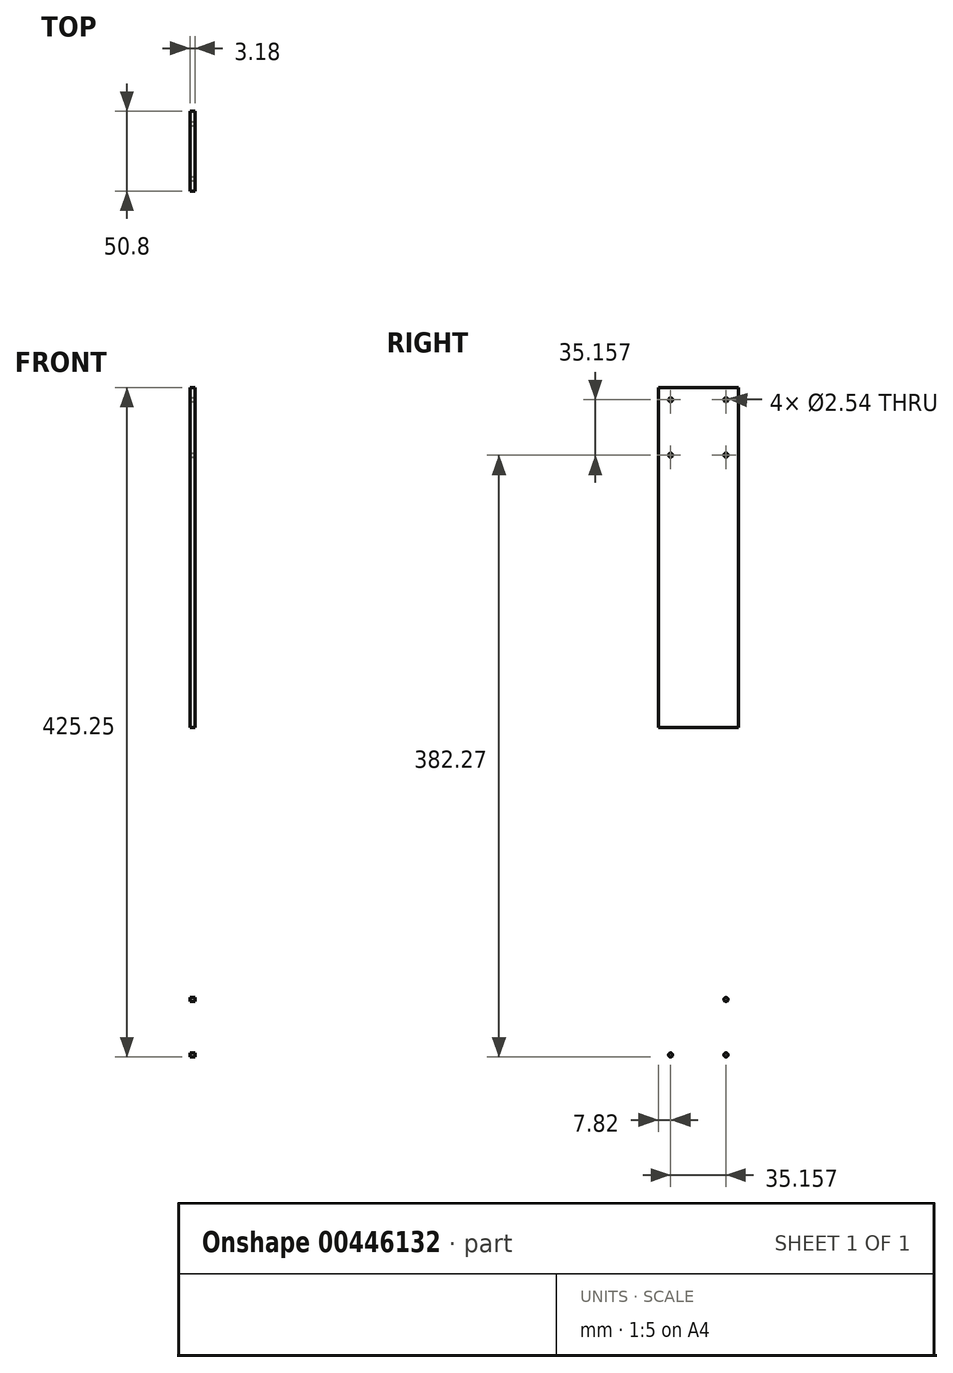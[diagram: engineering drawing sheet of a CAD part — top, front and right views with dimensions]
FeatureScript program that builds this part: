
annotation { "Feature Type Name" : "Feature", "Feature Type Description" : "" }
export const myFeature = defineFeature(function(context is Context, id is Id, definition is map)
    precondition{}
    {
        {
            var Q0;
            Q0=qCreatedBy(makeId("Right.planeOp"),FACE);
            var sketch = newSketch(context, id + "F0", { "sketchPlane" : qUnion([Q0])});
            skLineSegment(sketch, "E0.bottom", {"start": v(-32.7, 346.88) * mm, "end": v(18.1, 346.88) * mm});
            skLineSegment(sketch, "E0.top", {"start": v(-32.7, -84.92) * mm, "end": v(18.1, -84.92) * mm});
            skLineSegment(sketch, "E0.left", {"start": v(-32.7, 346.88) * mm, "end": v(-32.7, -84.92) * mm});
            skLineSegment(sketch, "E0.right", {"start": v(18.1, 346.88) * mm, "end": v(18.1, -84.92) * mm});
            skSolve(sketch);
        }
        {
            var Q0;
            Q0=makeQuery(id+"F0.imprint","IMPRINT",FACE,{"disambiguationData":[TD([[makeQuery(id+"F0.imprint","IMPRINT",EDGE,{"derivedFrom":sQuery(id+"F0.wireOp",EDGE,"E0.bottom")}),-1.0]])]});
            extrude(context, id + "F1", {"entities" : qUnion([Q0]), "depth" : 3.17 * mm});
        }
        {
            var Q0;
            Q0=makeQuery(id+"F1.opExtrude","CAP_FACE",FACE,{"disambiguationData":[OSD([sQuery(id+"F0.wireOp",EDGE,"E0.bottom"),sQuery(id+"F0.wireOp",EDGE,"E0.top"),sQuery(id+"F0.wireOp",EDGE,"E0.left"),sQuery(id+"F0.wireOp",EDGE,"E0.right")])],"isStart":false});
            var sketch = newSketch(context, id + "F2", { "sketchPlane" : qUnion([Q0])});
            skPoint(sketch, "E1.centerSnap0", {"position": v(-7.3, 346.88) * mm});
            skLineSegment(sketch, "E2.bottom", {"start": v(10.28, 339.06) * mm, "end": v(-24.88, 339.06) * mm});
            skLineSegment(sketch, "E2.top", {"start": v(10.28, 303.9) * mm, "end": v(-24.88, 303.9) * mm});
            skLineSegment(sketch, "E2.left", {"start": v(10.28, 339.06) * mm, "end": v(10.28, 303.9) * mm});
            skLineSegment(sketch, "E2.right", {"start": v(-24.88, 339.06) * mm, "end": v(-24.88, 303.9) * mm});
            skPoint(sketch, "E2.middle", {"position": v(-7.3, 321.48) * mm});
            skCircle(sketch, "E3", {"center": v(-24.88, 339.06) * mm, "radius": 1.27 * mm});
            skCircle(sketch, "E4", {"center": v(-24.88, 303.9) * mm, "radius": 1.27 * mm});
            skCircle(sketch, "E5", {"center": v(10.28, 303.9) * mm, "radius": 1.27 * mm});
            skCircle(sketch, "E6", {"center": v(10.28, 339.06) * mm, "radius": 1.27 * mm});
            skLineSegment(sketch, "E7", {"start": v(-32.7, 130.98) * mm, "end": v(18.1, 130.98) * mm});
            skCircle(sketch, "E8.MirrorC", {"center": v(-24.88, -41.94) * mm, "radius": 1.27 * mm});
            skCircle(sketch, "E9.MirrorC", {"center": v(10.28, -41.94) * mm, "radius": 1.27 * mm});
            skLineSegment(sketch, "E10.MirrorCS", {"start": v(10.28, -41.94) * mm, "end": v(-24.88, -41.94) * mm});
            skLineSegment(sketch, "E11.MirrorCS", {"start": v(-24.88, -77.1) * mm, "end": v(-24.88, -41.94) * mm});
            skCircle(sketch, "E12.MirrorC", {"center": v(10.28, -77.1) * mm, "radius": 1.27 * mm});
            skCircle(sketch, "E13.MirrorC", {"center": v(-24.88, -77.1) * mm, "radius": 1.27 * mm});
            skSolve(sketch);
        }
        {
            var Q0;
            {var subQ0=sQuery(id+"F2.wireOp",EDGE,"E2.right");var subQ1=sQuery(id+"F2.wireOp",EDGE,"E2.top");var subQ2=makeQuery(id+"F2.imprint","INTERSECT",VERTEX,{"derivedFrom":[subQ1,subQ0]});Q0=makeQuery(id+"F2.imprint","IMPRINT",FACE,{"disambiguationData":[TD([[makeQuery(id+"F2.imprint","IMPRINT",EDGE,{"disambiguationData":[TD([[subQ2,1.0]])],"derivedFrom":subQ1}),1.0]])]});}
            var Q1;
            {var subQ0=sQuery(id+"F2.wireOp",EDGE,"E2.right");var subQ1=sQuery(id+"F2.wireOp",EDGE,"E2.top");var subQ2=makeQuery(id+"F2.imprint","INTERSECT",VERTEX,{"derivedFrom":[subQ1,subQ0]});Q1=makeQuery(id+"F2.imprint","IMPRINT",FACE,{"disambiguationData":[TD([[makeQuery(id+"F2.imprint","IMPRINT",EDGE,{"disambiguationData":[TD([[subQ2,1.0]])],"derivedFrom":subQ1}),-1.0]])]});}
            var Q2;
            {var subQ0=sQuery(id+"F2.wireOp",EDGE,"E2.right");var subQ1=sQuery(id+"F2.wireOp",EDGE,"E2.bottom");var subQ2=makeQuery(id+"F2.imprint","INTERSECT",VERTEX,{"derivedFrom":[subQ1,subQ0]});Q2=makeQuery(id+"F2.imprint","IMPRINT",FACE,{"disambiguationData":[TD([[makeQuery(id+"F2.imprint","IMPRINT",EDGE,{"disambiguationData":[TD([[subQ2,1.0]])],"derivedFrom":subQ1}),1.0]])]});}
            var Q3;
            {var subQ0=sQuery(id+"F2.wireOp",EDGE,"E2.right");var subQ1=sQuery(id+"F2.wireOp",EDGE,"E2.bottom");var subQ2=makeQuery(id+"F2.imprint","INTERSECT",VERTEX,{"derivedFrom":[subQ1,subQ0]});Q3=makeQuery(id+"F2.imprint","IMPRINT",FACE,{"disambiguationData":[TD([[makeQuery(id+"F2.imprint","IMPRINT",EDGE,{"disambiguationData":[TD([[subQ2,1.0]])],"derivedFrom":subQ1}),-1.0]])]});}
            var Q4;
            {var subQ0=sQuery(id+"F2.wireOp",EDGE,"E2.left");var subQ1=sQuery(id+"F2.wireOp",EDGE,"E2.bottom");var subQ2=makeQuery(id+"F2.imprint","INTERSECT",VERTEX,{"derivedFrom":[subQ1,subQ0]});Q4=makeQuery(id+"F2.imprint","IMPRINT",FACE,{"disambiguationData":[TD([[makeQuery(id+"F2.imprint","IMPRINT",EDGE,{"disambiguationData":[TD([[subQ2,-1.0]])],"derivedFrom":subQ1}),-1.0]])]});}
            var Q5;
            {var subQ0=sQuery(id+"F2.wireOp",EDGE,"E2.left");var subQ1=sQuery(id+"F2.wireOp",EDGE,"E2.bottom");var subQ2=makeQuery(id+"F2.imprint","INTERSECT",VERTEX,{"derivedFrom":[subQ1,subQ0]});Q5=makeQuery(id+"F2.imprint","IMPRINT",FACE,{"disambiguationData":[TD([[makeQuery(id+"F2.imprint","IMPRINT",EDGE,{"disambiguationData":[TD([[subQ2,-1.0]])],"derivedFrom":subQ1}),1.0]])]});}
            var Q6;
            {var subQ0=sQuery(id+"F2.wireOp",EDGE,"E2.left");var subQ1=sQuery(id+"F2.wireOp",EDGE,"E2.top");var subQ2=makeQuery(id+"F2.imprint","INTERSECT",VERTEX,{"derivedFrom":[subQ1,subQ0]});Q6=makeQuery(id+"F2.imprint","IMPRINT",FACE,{"disambiguationData":[TD([[makeQuery(id+"F2.imprint","IMPRINT",EDGE,{"disambiguationData":[TD([[subQ2,-1.0]])],"derivedFrom":subQ1}),1.0]])]});}
            var Q7;
            {var subQ0=sQuery(id+"F2.wireOp",EDGE,"E2.left");var subQ1=sQuery(id+"F2.wireOp",EDGE,"E2.top");var subQ2=makeQuery(id+"F2.imprint","INTERSECT",VERTEX,{"derivedFrom":[subQ1,subQ0]});Q7=makeQuery(id+"F2.imprint","IMPRINT",FACE,{"disambiguationData":[TD([[makeQuery(id+"F2.imprint","IMPRINT",EDGE,{"disambiguationData":[TD([[subQ2,-1.0]])],"derivedFrom":subQ1}),-1.0]])]});}
            var Q8;
            Q8=makeQuery(id+"F2.imprint","IMPRINT",FACE,{"disambiguationData":[TD([[makeQuery(id+"F2.imprint","IMPRINT",EDGE,{"derivedFrom":sQuery(id+"F2.wireOp",EDGE,"E13.MirrorC")}),-1.0]])]});
            var Q9;
            {var subQ0=sQuery(id+"F2.wireOp",EDGE,"E11.MirrorCS");var subQ1=sQuery(id+"F2.wireOp",EDGE,"E10.MirrorCS");var subQ2=makeQuery(id+"F2.imprint","INTERSECT",VERTEX,{"derivedFrom":[subQ1,subQ0]});Q9=makeQuery(id+"F2.imprint","IMPRINT",FACE,{"disambiguationData":[TD([[makeQuery(id+"F2.imprint","IMPRINT",EDGE,{"disambiguationData":[TD([[subQ2,1.0]])],"derivedFrom":subQ1}),1.0]])]});}
            var Q10;
            {var subQ0=sQuery(id+"F2.wireOp",EDGE,"E11.MirrorCS");var subQ1=sQuery(id+"F2.wireOp",EDGE,"E10.MirrorCS");var subQ2=makeQuery(id+"F2.imprint","INTERSECT",VERTEX,{"derivedFrom":[subQ1,subQ0]});Q10=makeQuery(id+"F2.imprint","IMPRINT",FACE,{"disambiguationData":[TD([[makeQuery(id+"F2.imprint","IMPRINT",EDGE,{"disambiguationData":[TD([[subQ2,1.0]])],"derivedFrom":subQ1}),-1.0]])]});}
            var Q11;
            Q11=makeQuery(id+"F2.imprint","IMPRINT",FACE,{"disambiguationData":[TD([[makeQuery(id+"F2.imprint","IMPRINT",EDGE,{"derivedFrom":sQuery(id+"F2.wireOp",EDGE,"E9.MirrorC")}),-1.0]])]});
            var Q12;
            Q12=makeQuery(id+"F2.imprint","IMPRINT",FACE,{"disambiguationData":[TD([[makeQuery(id+"F2.imprint","IMPRINT",EDGE,{"derivedFrom":sQuery(id+"F2.wireOp",EDGE,"E12.MirrorC")}),-1.0]])]});
            extrude(context, id + "F3", {"entities" : qUnion([Q0, Q1, Q2, Q3, Q4, Q5, Q6, Q7, Q8, Q9, Q10, Q11, Q12]), "operationType" : NewBodyOperationType.REMOVE, "endBound" : BoundingType.THROUGH_ALL, "oppositeDirection" : true, "depth" : 121.92 * mm});
        }
    });
